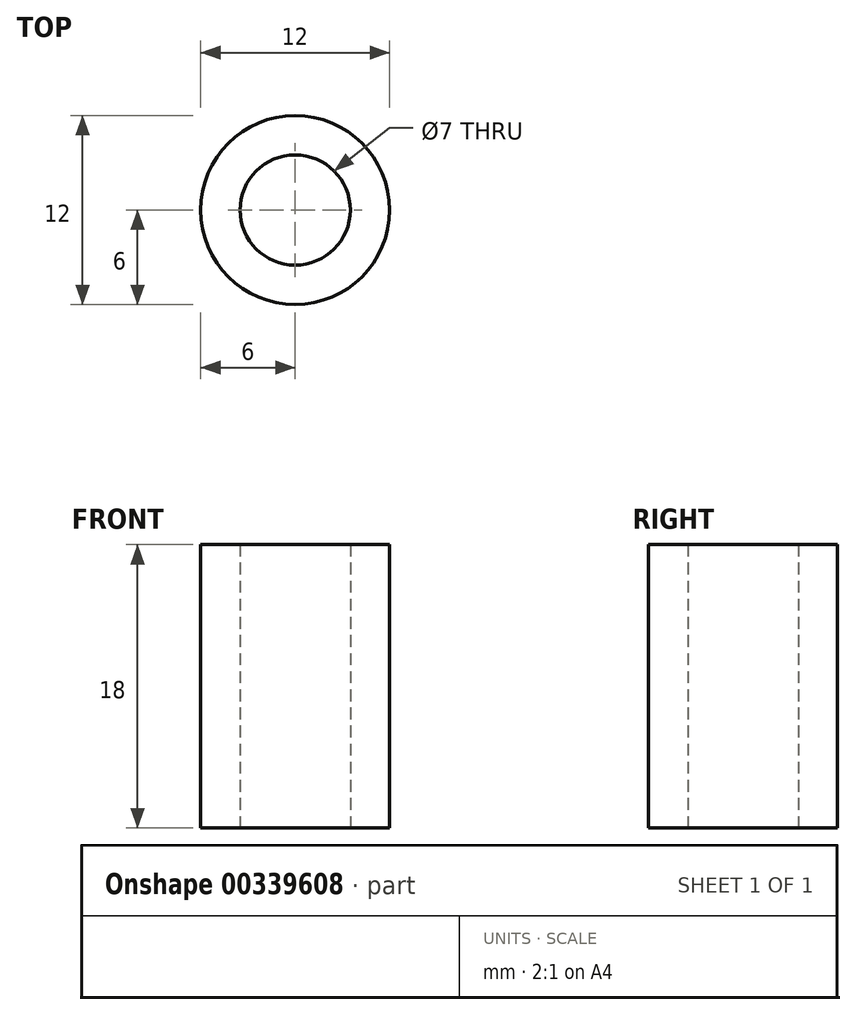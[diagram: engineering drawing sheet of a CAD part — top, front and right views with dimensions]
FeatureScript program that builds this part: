
annotation { "Feature Type Name" : "Feature", "Feature Type Description" : "" }
export const myFeature = defineFeature(function(context is Context, id is Id, definition is map)
    precondition{}
    {
        {
            var Q0;
            Q0=qCreatedBy(makeId("Top.planeOp"),FACE);
            var sketch = newSketch(context, id + "F0", { "sketchPlane" : qUnion([Q0])});
            skCircle(sketch, "E0", {"center": v(0, 0) * mm, "radius": 3.5 * mm});
            skCircle(sketch, "E1", {"center": v(0, 0) * mm, "radius": 6 * mm});
            skSolve(sketch);
        }
        {
            var Q0;
            Q0=qSketchRegion(id+"F0",true);
            extrude(context, id + "F1", {"entities" : qUnion([Q0]), "depth" : 18 * mm});
        }
    });
